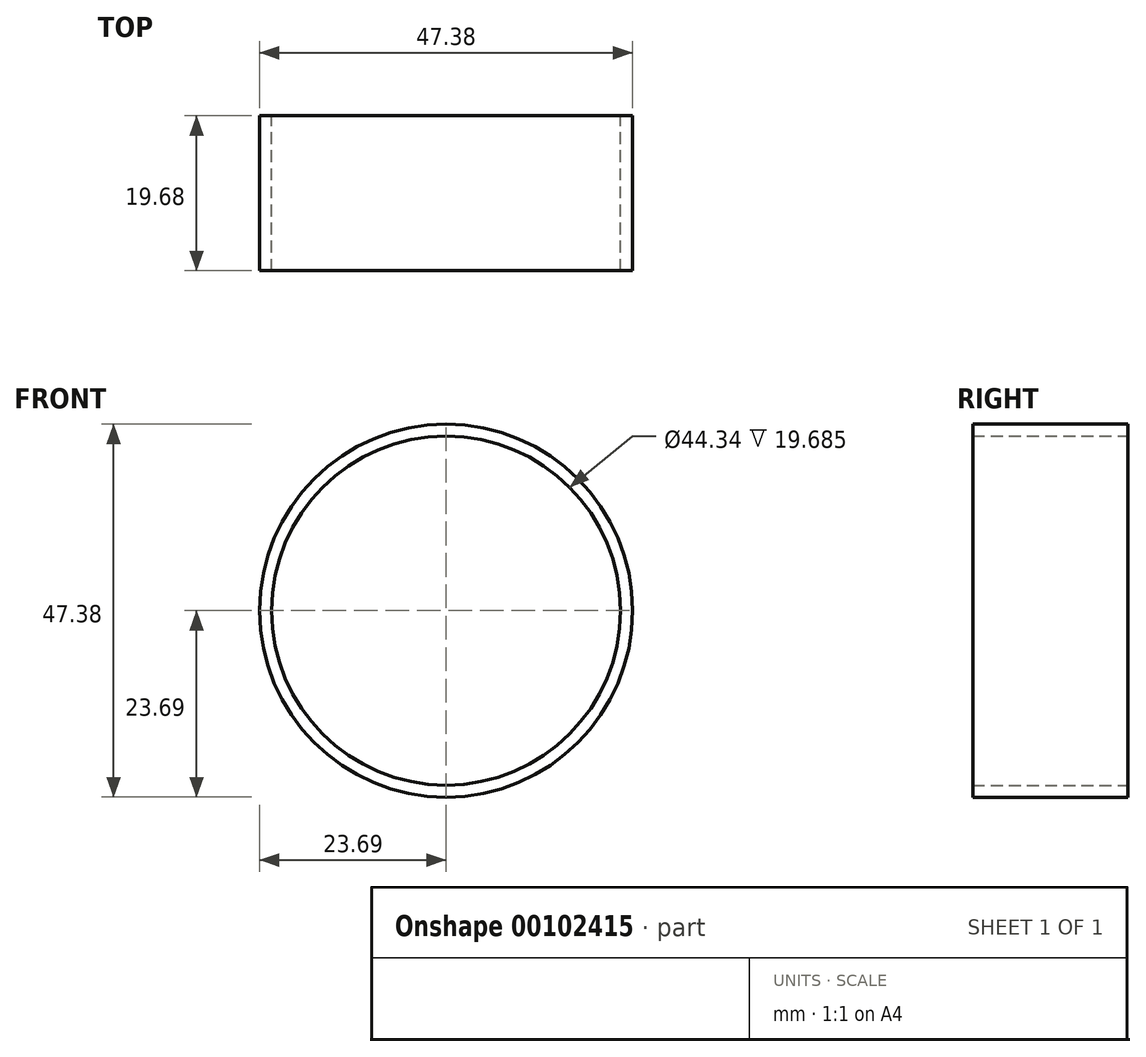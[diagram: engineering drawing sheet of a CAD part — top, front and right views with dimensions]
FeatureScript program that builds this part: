
annotation { "Feature Type Name" : "Feature", "Feature Type Description" : "" }
export const myFeature = defineFeature(function(context is Context, id is Id, definition is map)
    precondition{}
    {
        {
            var Q0;
            Q0=qCreatedBy(makeId("Right.planeOp"),FACE);
            var sketch = newSketch(context, id + "F0", { "sketchPlane" : qUnion([Q0])});
            skLineSegment(sketch, "E0.bottom", {"start": v(-9.84, 22.17) * mm, "end": v(9.84, 22.17) * mm});
            skLineSegment(sketch, "E0.top", {"start": v(-9.84, 23.7) * mm, "end": v(9.84, 23.7) * mm});
            skLineSegment(sketch, "E0.left", {"start": v(-9.84, 22.17) * mm, "end": v(-9.84, 23.7) * mm});
            skLineSegment(sketch, "E0.right", {"start": v(9.84, 22.17) * mm, "end": v(9.84, 23.7) * mm});
            skLineSegment(sketch, "E1", {"start": v(29.43, 0) * mm, "end": v(-37.51, 0) * mm, "construction": true});
            skSolve(sketch);
        }
        {
            var Q0;
            Q0=makeQuery(id+"F0.imprint","IMPRINT",FACE,{"disambiguationData":[TD([[makeQuery(id+"F0.imprint","IMPRINT",EDGE,{"derivedFrom":sQuery(id+"F0.wireOp",EDGE,"E0.bottom")}),1.0]])]});
            var Q1;
            Q1=sQuery(id+"F0.wireOp",EDGE,"E1");
            revolve(context, id + "F1", {"entities" : qUnion([Q0]), "axis" : qUnion([Q1]), "revolveType" : RevolveType.FULL});
        }
    });
